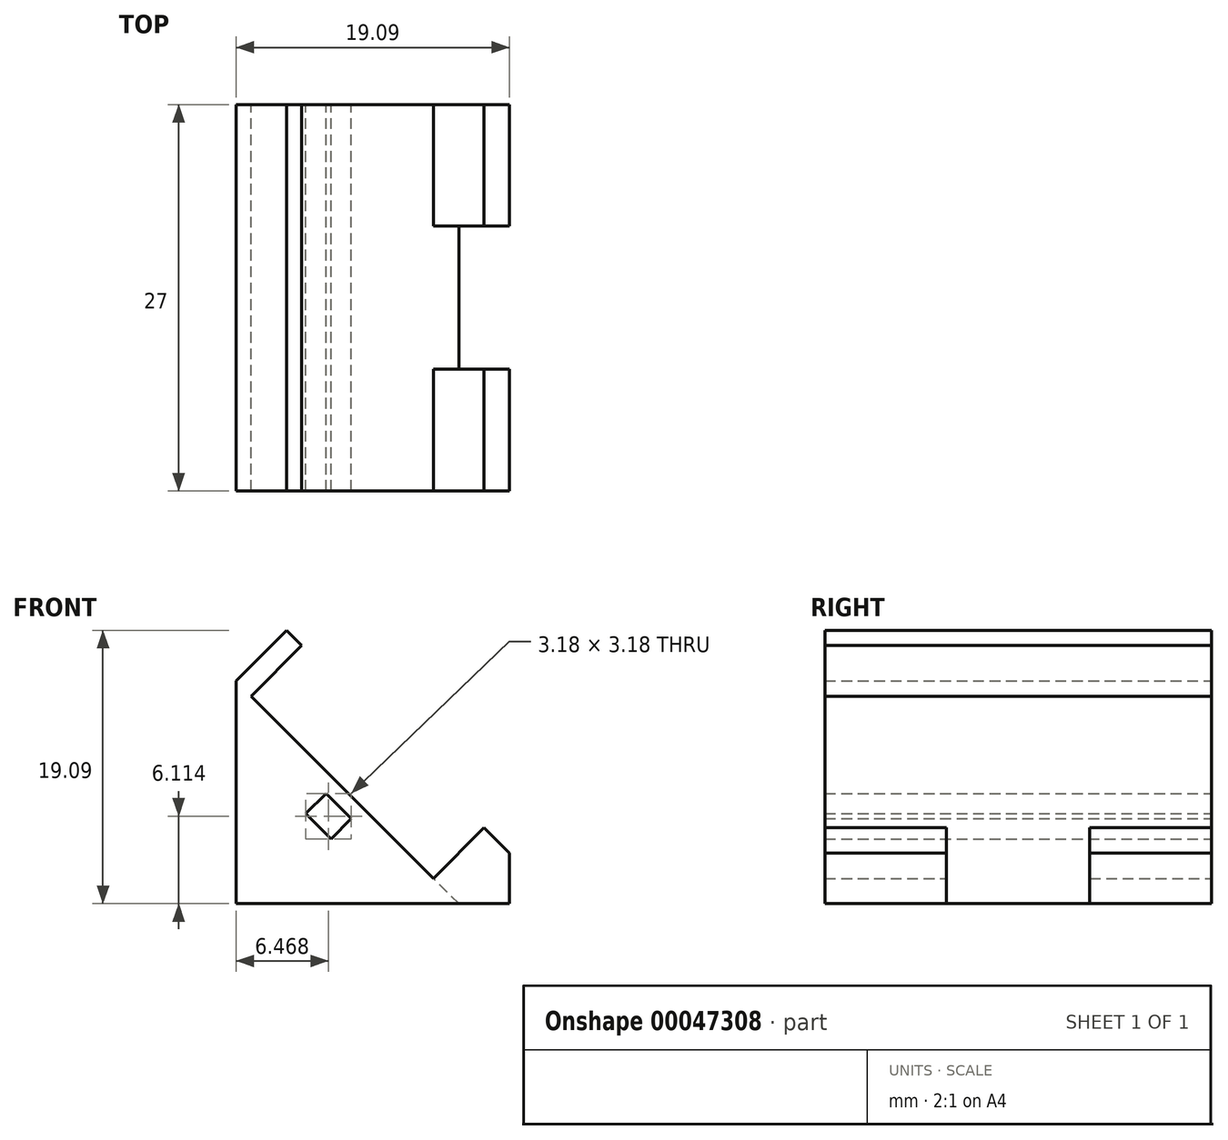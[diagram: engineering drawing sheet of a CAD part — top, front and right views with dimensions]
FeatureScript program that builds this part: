
annotation { "Feature Type Name" : "Feature", "Feature Type Description" : "" }
export const myFeature = defineFeature(function(context is Context, id is Id, definition is map)
    precondition{}
    {
        {
            var Q0;
            Q0=qCreatedBy(makeId("Front.planeOp"),FACE);
            var sketch = newSketch(context, id + "F0", { "sketchPlane" : qUnion([Q0])});
            skLineSegment(sketch, "E0", {"start": v(0, 0) * mm, "end": v(0, 15.56) * mm});
            skLineSegment(sketch, "E1", {"start": v(0, 15.56) * mm, "end": v(15.56, 0) * mm});
            skLineSegment(sketch, "E2", {"start": v(15.56, 0) * mm, "end": v(19.1, 3.54) * mm});
            skLineSegment(sketch, "E3", {"start": v(19.1, 3.54) * mm, "end": v(17.32, 5.3) * mm});
            skLineSegment(sketch, "E4", {"start": v(17.32, 5.3) * mm, "end": v(13.79, 1.77) * mm});
            skLineSegment(sketch, "E5", {"start": v(0, 15.56) * mm, "end": v(3.54, 19.1) * mm});
            skLineSegment(sketch, "E6", {"start": v(3.54, 19.1) * mm, "end": v(4.6, 18.03) * mm});
            skLineSegment(sketch, "E7", {"start": v(4.6, 18.03) * mm, "end": v(1.06, 14.5) * mm});
            skLineSegment(sketch, "E8", {"start": v(0, 0) * mm, "end": v(15.56, 0) * mm});
            skLineSegment(sketch, "E9", {"start": v(19.1, 3.54) * mm, "end": v(19.1, 0) * mm});
            skLineSegment(sketch, "E10", {"start": v(19.1, 0) * mm, "end": v(15.56, 0) * mm});
            skLineSegment(sketch, "E11", {"start": v(6.3, 7.7) * mm, "end": v(8.06, 5.94) * mm});
            skLineSegment(sketch, "E12", {"start": v(8.06, 5.94) * mm, "end": v(6.64, 4.52) * mm});
            skLineSegment(sketch, "E13", {"start": v(6.64, 4.52) * mm, "end": v(4.88, 6.3) * mm});
            skLineSegment(sketch, "E14", {"start": v(4.88, 6.3) * mm, "end": v(6.3, 7.7) * mm});
            skSolve(sketch);
        }
        {
            var Q0;
            Q0 = qSketchRegion(id + "F0", true);
            extrude(context, id + "F1", {"entities" : qUnion([Q0]), "depth" : 27 * mm});
        }
        {
            var Q0;
            Q0=makeQuery(id+"F1.opExtrude","SWEPT_FACE",FACE,{"disambiguationData":[OSD([sQuery(id+"F0.wireOp",EDGE,"E7")])]});
            var sketch = newSketch(context, id + "F2", { "sketchPlane" : qUnion([Q0])});
            skLineSegment(sketch, "E15", {"start": v(16, 21.5) * mm, "end": v(11, 21.5) * mm});
            skLineSegment(sketch, "E16", {"start": v(11, 21.5) * mm, "end": v(11, 5.5) * mm});
            skLineSegment(sketch, "E17", {"start": v(11, 5.5) * mm, "end": v(16, 5.5) * mm});
            skLineSegment(sketch, "E18", {"start": v(16, 5.5) * mm, "end": v(16, 21.5) * mm});
            skSolve(sketch);
        }
        {
            var Q0;
            Q0 = qSketchRegion(id + "F2", true);
            extrude(context, id + "F3", {"entities" : qUnion([Q0]), "operationType" : NewBodyOperationType.REMOVE, "oppositeDirection" : true, "depth" : 25 * mm});
        }
        {
            var Q0;
            Q0=makeQuery(id+"F1.opExtrude","SWEPT_FACE",FACE,{"disambiguationData":[OSD([sQuery(id+"F0.wireOp",EDGE,"E4")])]});
            var sketch = newSketch(context, id + "F4", { "sketchPlane" : qUnion([Q0])});
            skLineSegment(sketch, "E19", {"start": v(8.5, 11) * mm, "end": v(8.5, 16) * mm});
            skLineSegment(sketch, "E20", {"start": v(8.5, 16) * mm, "end": v(18.5, 16) * mm});
            skLineSegment(sketch, "E21", {"start": v(18.5, 16) * mm, "end": v(18.5, 11) * mm});
            skPoint(sketch, "E21.endSnap0", {"position": v(13.5, 11) * mm});
            skLineSegment(sketch, "E22", {"start": v(18.5, 11) * mm, "end": v(8.5, 11) * mm});
            skSolve(sketch);
        }
        {
            var Q0;
            Q0 = qSketchRegion(id + "F4", true);
            extrude(context, id + "F5", {"entities" : qUnion([Q0]), "operationType" : NewBodyOperationType.REMOVE, "oppositeDirection" : true, "depth" : 25 * mm});
        }
    });
